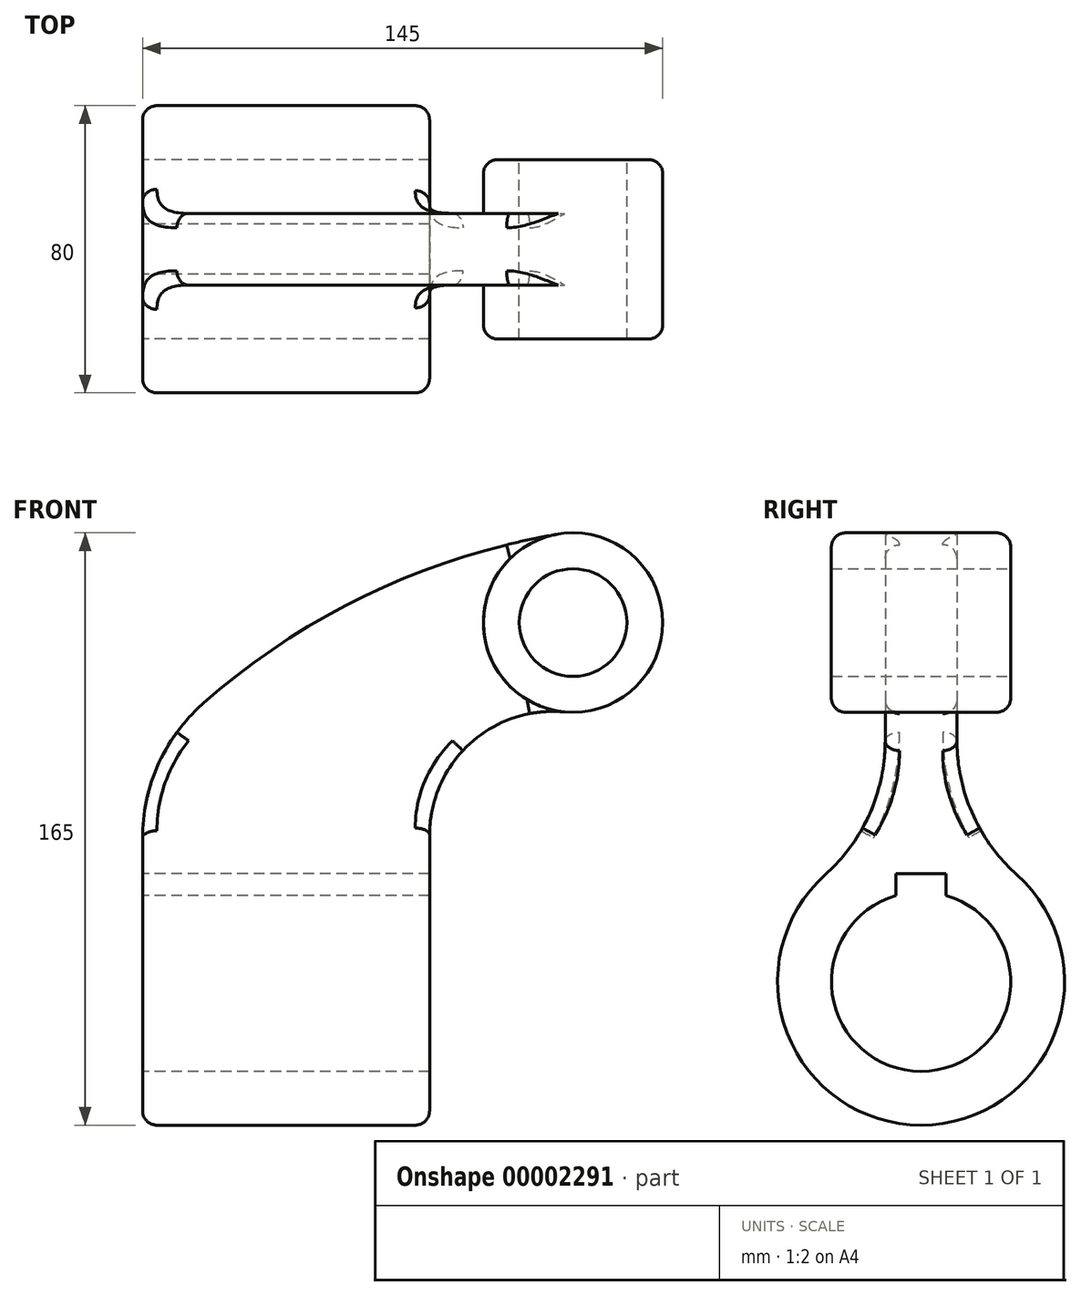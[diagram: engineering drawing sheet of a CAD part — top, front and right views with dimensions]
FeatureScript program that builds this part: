
annotation { "Feature Type Name" : "Feature", "Feature Type Description" : "" }
export const myFeature = defineFeature(function(context is Context, id is Id, definition is map)
    precondition{}
    {
        {
            var Q0;
            Q0=qCreatedBy(makeId("Front.planeOp"),FACE);
            var sketch = newSketch(context, id + "F0", { "sketchPlane" : qUnion([Q0])});
            skLineSegment(sketch, "E0", {"start": v(0, 0) * mm, "end": v(80, 0) * mm});
            skLineSegment(sketch, "E1", {"start": v(80, 0) * mm, "end": v(80, 40.8) * mm});
            skLineSegment(sketch, "E2", {"start": v(0, 0) * mm, "end": v(0, 40) * mm});
            skArc(sketch, "E3", {"start": v(0, 40) * mm, "mid": v(4.43, 60.58) * mm, "end": v(16.95, 77.52) * mm});
            skArc(sketch, "E4", {"start": v(16.95, 77.52) * mm, "mid": v(63.1, 107.99) * mm, "end": v(115.84, 124.65) * mm});
            skCircle(sketch, "E5", {"center": v(120, 100) * mm, "radius": 25 * mm});
            skArc(sketch, "E6", {"start": v(80, 40.8) * mm, "mid": v(91.26, 66.28) * mm, "end": v(117.67, 75.1) * mm});
            skCircle(sketch, "E7", {"center": v(120, 100) * mm, "radius": 15 * mm});
            skSolve(sketch);
        }
        {
            var Q0;
            Q0=qCreatedBy(makeId("Right.planeOp"),FACE);
            var sketch = newSketch(context, id + "F1", { "sketchPlane" : qUnion([Q0])});
            skCircle(sketch, "E8", {"center": v(0, 0) * mm, "radius": 40 * mm});
            skArc(sketch, "E9", {"start": v(-7, 24) * mm, "mid": v(0, -25) * mm, "end": v(7, 24) * mm});
            skLineSegment(sketch, "E10", {"start": v(0, 0) * mm, "end": v(0, -60.12) * mm, "construction": true});
            skLineSegment(sketch, "E11", {"start": v(0, 30) * mm, "end": v(7, 30) * mm});
            skLineSegment(sketch, "E12", {"start": v(7, 30) * mm, "end": v(7, 24) * mm});
            skLineSegment(sketch, "E13.0.MirrorCS", {"start": v(-7, 30) * mm, "end": v(-7, 24) * mm});
            skLineSegment(sketch, "E13.1.MirrorCS", {"start": v(0, 30) * mm, "end": v(-7, 30) * mm});
            skSolve(sketch);
        }
        {
            var Q0;
            Q0=makeQuery(id+"F1.imprint","IMPRINT",FACE,{"disambiguationData":[TD([[makeQuery(id+"F1.imprint","IMPRINT",EDGE,{"derivedFrom":sQuery(id+"F1.wireOp",EDGE,"E8")}),1.0]])]});
            var Q1;
            Q1=makeQuery(id+"F1.imprint","IMPRINT",FACE,{"disambiguationData":[TD([[makeQuery(id+"F1.imprint","IMPRINT",EDGE,{"derivedFrom":sQuery(id+"F1.wireOp",EDGE,"E9")}),1.0]])]});
            var Q2;
            Q2=sQuery(id+"F1.wireOp",EDGE,"E8");
            extrude(context, id + "F2", {"entities" : qUnion([Q0, Q1]), "surfaceEntities" : qUnion([Q2]), "depth" : 80 * mm});
        }
        {
            var Q0;
            Q0=makeQuery(id+"F0.imprint","IMPRINT",FACE,{"disambiguationData":[TD([[makeQuery(id+"F0.imprint","IMPRINT",EDGE,{"derivedFrom":sQuery(id+"F0.wireOp",EDGE,"E7")}),-1.0]])]});
            extrude(context, id + "F3", {"entities" : qUnion([Q0]), "depth" : 50 * mm, "symmetric" : true});
        }
        {
            var Q0;
            Q0=makeQuery(id+"F0.imprint","IMPRINT",FACE,{"disambiguationData":[TD([[makeQuery(id+"F0.imprint","IMPRINT",EDGE,{"derivedFrom":sQuery(id+"F0.wireOp",EDGE,"E0")}),1.0]])]});
            extrude(context, id + "F4", {"entities" : qUnion([Q0]), "depth" : 20 * mm, "symmetric" : true});
        }
        {
            var Q0;
            Q0=makeQuery(id+"F4.opExtrude","SWEPT_BODY",BODY,{"disambiguationData":[OSD([sQuery(id+"F0.wireOp",EDGE,"E0"),sQuery(id+"F0.wireOp",EDGE,"E1"),sQuery(id+"F0.wireOp",EDGE,"E2"),sQuery(id+"F0.wireOp",EDGE,"E3"),sQuery(id+"F0.wireOp",EDGE,"E4"),sQuery(id+"F0.wireOp",EDGE,"E5"),sQuery(id+"F0.wireOp",EDGE,"E6")])]});
            var Q1;
            Q1=makeQuery(id+"F2.opExtrude","SWEPT_BODY",BODY,{"disambiguationData":[OSD([sQuery(id+"F1.wireOp",EDGE,"E8")])]});
            var Q2;
            Q2=makeQuery(id+"F3.opExtrude","SWEPT_BODY",BODY,{"disambiguationData":[OSD([sQuery(id+"F0.wireOp",EDGE,"E5"),sQuery(id+"F0.wireOp",EDGE,"E7")])]});
            booleanBodies(context, id + "F5", {"operationType" : BooleanOperationType.UNION, "tools" : qUnion([Q0, Q1, Q2])});
        }
        {
            var Q0;
            Q0=makeQuery(id+"F1.imprint","IMPRINT",FACE,{"disambiguationData":[TD([[makeQuery(id+"F1.imprint","IMPRINT",EDGE,{"derivedFrom":sQuery(id+"F1.wireOp",EDGE,"E9")}),1.0]])]});
            extrude(context, id + "F6", {"entities" : qUnion([Q0]), "operationType" : NewBodyOperationType.REMOVE, "endBound" : BoundingType.THROUGH_ALL, "depth" : 25 * mm});
        }
        {
            var Q0;
            Q0=makeQuery(id+"F5.opBoolean","INTERSECT",EDGE,{"derivedFrom":[makeQuery(id+"F2.opExtrude","SWEPT_FACE",FACE,{"disambiguationData":[OSD([sQuery(id+"F1.wireOp",EDGE,"E8")])]}),makeQuery(id+"F4.opExtrude","CAP_FACE",FACE,{"disambiguationData":[OSD([sQuery(id+"F0.wireOp",EDGE,"E0"),sQuery(id+"F0.wireOp",EDGE,"E1"),sQuery(id+"F0.wireOp",EDGE,"E2"),sQuery(id+"F0.wireOp",EDGE,"E3"),sQuery(id+"F0.wireOp",EDGE,"E4"),sQuery(id+"F0.wireOp",EDGE,"E5"),sQuery(id+"F0.wireOp",EDGE,"E6")])],"isStart":false})]});
            var Q1;
            Q1=makeQuery(id+"F5.opBoolean","INTERSECT",EDGE,{"derivedFrom":[makeQuery(id+"F2.opExtrude","SWEPT_FACE",FACE,{"disambiguationData":[OSD([sQuery(id+"F1.wireOp",EDGE,"E8")])]}),makeQuery(id+"F4.opExtrude","CAP_FACE",FACE,{"disambiguationData":[OSD([sQuery(id+"F0.wireOp",EDGE,"E0"),sQuery(id+"F0.wireOp",EDGE,"E1"),sQuery(id+"F0.wireOp",EDGE,"E2"),sQuery(id+"F0.wireOp",EDGE,"E3"),sQuery(id+"F0.wireOp",EDGE,"E4"),sQuery(id+"F0.wireOp",EDGE,"E5"),sQuery(id+"F0.wireOp",EDGE,"E6")])],"isStart":true})]});
            fillet(context, id + "F7", {"entities" : qUnion([Q0, Q1]), "radius" : 50 * mm, "tangentPropagation" : true, "allowEdgeOverflow" : false});
        }
        {
            var Q0;
            Q0=makeQuery(id+"F4.opExtrude","CAP_EDGE",EDGE,{"disambiguationData":[OSD([sQuery(id+"F0.wireOp",EDGE,"E5")])],"isStart":false});
            var Q1;
            Q1=makeQuery(id+"F4.opExtrude","CAP_EDGE",EDGE,{"disambiguationData":[OSD([sQuery(id+"F0.wireOp",EDGE,"E5")])],"isStart":true});
            var Q2;
            Q2=makeQuery(id+"F3.opExtrude","CAP_EDGE",EDGE,{"disambiguationData":[OSD([sQuery(id+"F0.wireOp",EDGE,"E5")])],"isStart":true});
            var Q3;
            Q3=makeQuery(id+"F3.opExtrude","CAP_EDGE",EDGE,{"disambiguationData":[OSD([sQuery(id+"F0.wireOp",EDGE,"E5")])],"isStart":false});
            var Q4;
            Q4=makeQuery(id+"F2.opExtrude","CAP_EDGE",EDGE,{"disambiguationData":[OSD([sQuery(id+"F1.wireOp",EDGE,"E8")])],"isStart":false});
            var Q5;
            {var subQ0=sQuery(id+"F0.wireOp",EDGE,"E3");Q5=makeQuery(id+"F7.opFillet","BLEND_EDGE",EDGE,{"blendedFrom":[makeQuery(id+"F5.opBoolean","INTERSECT",EDGE,{"derivedFrom":[makeQuery(id+"F2.opExtrude","SWEPT_FACE",FACE,{"disambiguationData":[OSD([sQuery(id+"F1.wireOp",EDGE,"E8")])]}),makeQuery(id+"F4.opExtrude","CAP_FACE",FACE,{"disambiguationData":[OSD([sQuery(id+"F0.wireOp",EDGE,"E0"),sQuery(id+"F0.wireOp",EDGE,"E1"),sQuery(id+"F0.wireOp",EDGE,"E2"),subQ0,sQuery(id+"F0.wireOp",EDGE,"E4"),sQuery(id+"F0.wireOp",EDGE,"E5"),sQuery(id+"F0.wireOp",EDGE,"E6")])],"isStart":true})]}),makeQuery(id+"F4.opExtrude","SWEPT_FACE",FACE,{"disambiguationData":[OSD([subQ0])]})],"blendedInto":[makeQuery(id+"F4.opExtrude","SWEPT_FACE",FACE,{"disambiguationData":[OSD([subQ0])]})]});}
            fillet(context, id + "F8", {"entities" : qUnion([Q0, Q1, Q2, Q3, Q4, Q5]), "radius" : 4 * mm, "tangentPropagation" : true, "allowEdgeOverflow" : false});
        }
    });
